# Revit family: FU_Inspec_Area_Radius_90_LB
name_source: partatom
category: Furniture
units: mm (PartAtom-declared; Revit-internal decimal feet)

## family parameters
Always vertical = Yes
Cut with Voids When Loaded = No
OmniClass Number = 23.40.20.00
OmniClass Title = General Furniture and Specialties
Room Calculation Point = No
Shared = No
Work Plane-Based = No

## types (3) — shared parameters
Assembly Code = E2020
Depth = 680 mm  [stored 2.23097 ft]
Description = Modular sofa unit on powder coated or chromed Ø22 mm steel tubing sled base. Corner unit with upholstered seat and low back, and built-in magnetic linking device.
Height = 830 mm  [stored 2.7231 ft]
Keynote = 46.B
Legs Material = Metal - Chrome - Polished
Manufacturer = Inspec
Model = area radius 90lb
URL = https://inspecfurniture.com
Weight = 13.9
Width = 1210 mm  [stored 3.96982 ft]
zero-valued in all types: Default Elevation

## per-type parameters (varying)
| type | Seat Material |
| Fabric - Bright Orange | Fabric - Woven - Bright Orange |
| Fabric - Dark Purple | Fabric - Woven - Dark Purple |
| Fabric - Dark Blue | Fabric - Woven - Dark Blue |

note: [stored X ft] marks values corroborated as IEEE doubles in the binary element streams (Revit-internal decimal feet)

## geometry (parser evidence)
native form markers: Blend x6, Sweep x3
no freeform markers — native parametric forms only
